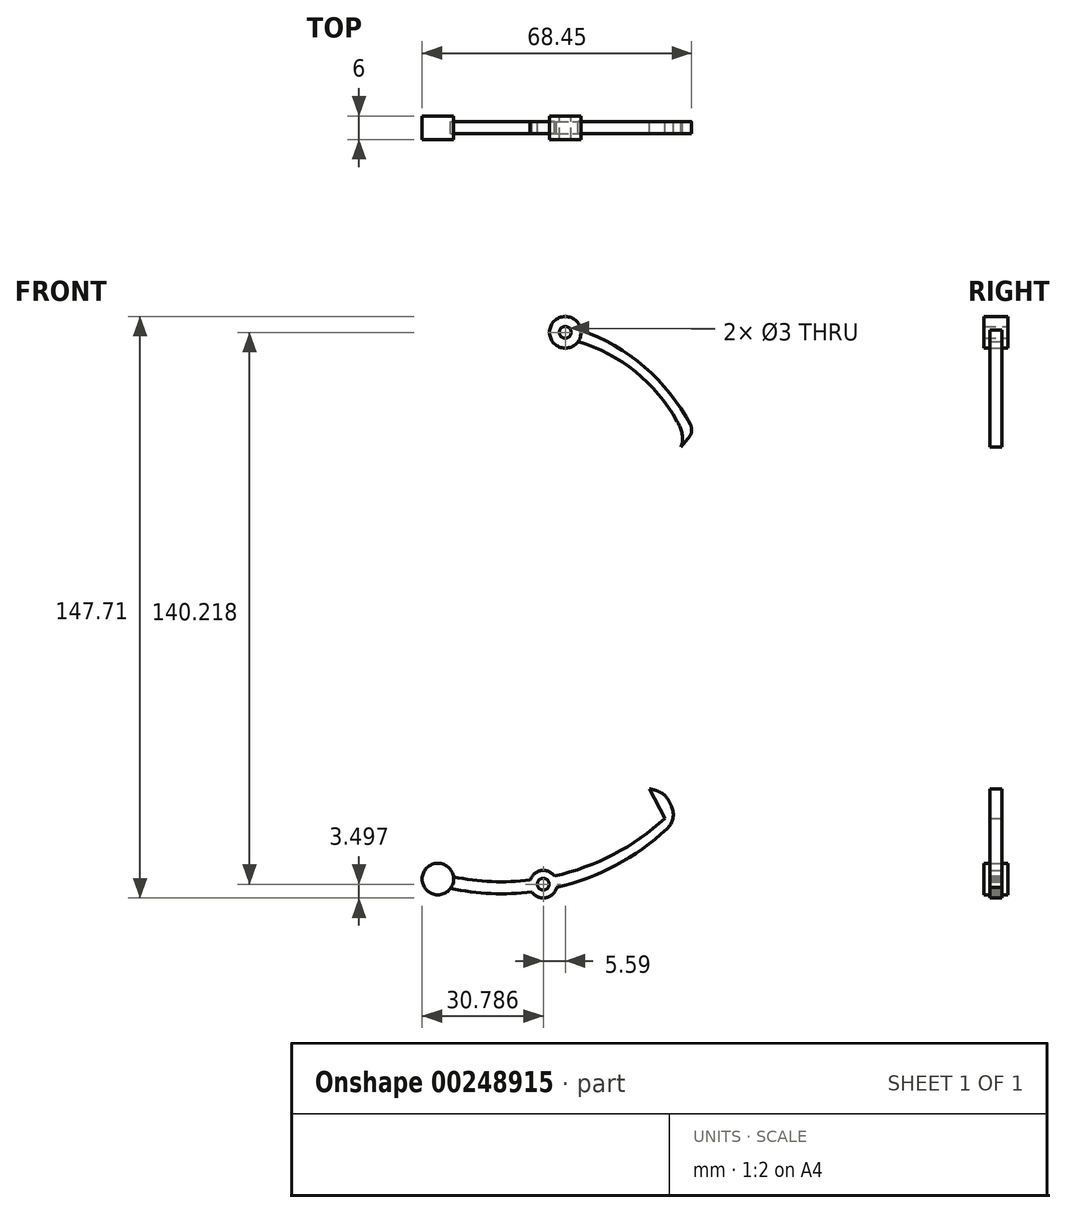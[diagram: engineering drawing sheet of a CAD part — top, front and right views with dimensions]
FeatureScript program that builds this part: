
annotation { "Feature Type Name" : "Feature", "Feature Type Description" : "" }
export const myFeature = defineFeature(function(context is Context, id is Id, definition is map)
    precondition{}
    {
        {
            var Q0;
            Q0=qCreatedBy(makeId("Front.planeOp"),FACE);
            var sketch = newSketch(context, id + "F0", { "sketchPlane" : qUnion([Q0])});
            skLineSegment(sketch, "E0", {"start": v(16.93, -54.43) * mm, "end": v(16.97, -54.42) * mm});
            skPoint(sketch, "E1.center", {"position": v(-0.03, 0) * mm});
            skLineSegment(sketch, "E2", {"start": v(0, 0) * mm, "end": v(-0.03, 0) * mm});
            skLineSegment(sketch, "E3", {"start": v(48.74, -18.05) * mm, "end": v(53.43, -19.79) * mm});
            skLineSegment(sketch, "E4", {"start": v(53.43, -19.79) * mm, "end": v(43.92, -27.8) * mm});
            skLineSegment(sketch, "E5.1.0", {"start": v(43.92, -27.8) * mm, "end": v(48.14, -30.47) * mm});
            skLineSegment(sketch, "E5.1.1", {"start": v(48.14, -30.47) * mm, "end": v(37.18, -36.33) * mm});
            skLineSegment(sketch, "E5.2.0", {"start": v(37.18, -36.33) * mm, "end": v(40.76, -39.82) * mm});
            skLineSegment(sketch, "E5.2.1", {"start": v(40.76, -39.82) * mm, "end": v(28.81, -43.27) * mm});
            skLineSegment(sketch, "E5.3.0", {"start": v(28.81, -43.27) * mm, "end": v(31.59, -47.43) * mm});
            skLineSegment(sketch, "E5.3.1", {"start": v(31.59, -47.43) * mm, "end": v(31.55, -47.43) * mm});
            skLineSegment(sketch, "E5.4.0", {"start": v(19.19, -48.32) * mm, "end": v(21.03, -52.96) * mm});
            skLineSegment(sketch, "E5.4.1", {"start": v(21.03, -52.96) * mm, "end": v(8.72, -51.26) * mm});
            skLineSegment(sketch, "E5.5.0", {"start": v(8.72, -51.26) * mm, "end": v(9.56, -56.19) * mm});
            skLineSegment(sketch, "E5.5.1", {"start": v(9.56, -56.19) * mm, "end": v(-2.13, -51.96) * mm});
            skLineSegment(sketch, "E5.6.0", {"start": v(-2.13, -51.96) * mm, "end": v(-2.33, -56.95) * mm});
            skLineSegment(sketch, "E5.6.1", {"start": v(-2.33, -56.95) * mm, "end": v(-12.89, -50.39) * mm});
            skLineSegment(sketch, "E5.7.0", {"start": v(-12.88, -50.39) * mm, "end": v(-14.12, -55.23) * mm});
            skLineSegment(sketch, "E5.7.1", {"start": v(-14.12, -55.23) * mm, "end": v(-23.08, -46.61) * mm});
            skLineSegment(sketch, "E5.8.0", {"start": v(-23.08, -46.61) * mm, "end": v(-25.3, -51.1) * mm});
            skLineSegment(sketch, "E5.8.1", {"start": v(-25.3, -51.1) * mm, "end": v(-32.27, -40.8) * mm});
            skLineSegment(sketch, "E5.9.0", {"start": v(-32.27, -40.8) * mm, "end": v(-35.37, -44.72) * mm});
            skLineSegment(sketch, "E5.9.1", {"start": v(-35.37, -44.72) * mm, "end": v(-40.05, -33.2) * mm});
            skLineSegment(sketch, "E5.10.0", {"start": v(-40.05, -33.2) * mm, "end": v(-43.9, -36.4) * mm});
            skLineSegment(sketch, "E5.10.1", {"start": v(-43.9, -36.4) * mm, "end": v(-46.08, -24.16) * mm});
            skLineSegment(sketch, "E5.11.0", {"start": v(-46.08, -24.16) * mm, "end": v(-50.5, -26.49) * mm});
            skLineSegment(sketch, "E5.11.1", {"start": v(-50.5, -26.49) * mm, "end": v(-50.1, -14.06) * mm});
            skLineSegment(sketch, "E5.12.0", {"start": v(-50.1, -14.06) * mm, "end": v(-54.9, -15.41) * mm});
            skLineSegment(sketch, "E5.12.1", {"start": v(-54.9, -15.41) * mm, "end": v(-51.92, -3.34) * mm});
            skLineSegment(sketch, "E5.13.0", {"start": v(-51.92, -3.34) * mm, "end": v(-56.91, -3.67) * mm});
            skLineSegment(sketch, "E5.13.1", {"start": v(-56.91, -3.67) * mm, "end": v(-51.48, 7.52) * mm});
            skLineSegment(sketch, "E5.14.0", {"start": v(-51.48, 7.52) * mm, "end": v(-56.43, 8.24) * mm});
            skLineSegment(sketch, "E5.14.1", {"start": v(-56.43, 8.24) * mm, "end": v(-48.8, 18.05) * mm});
            skLineSegment(sketch, "E5.15.0", {"start": v(-48.8, 18.05) * mm, "end": v(-53.49, 19.79) * mm});
            skLineSegment(sketch, "E5.15.1", {"start": v(-53.49, 19.79) * mm, "end": v(-43.98, 27.8) * mm});
            skLineSegment(sketch, "E5.16.0", {"start": v(-43.98, 27.8) * mm, "end": v(-48.2, 30.47) * mm});
            skLineSegment(sketch, "E5.16.1", {"start": v(-48.2, 30.47) * mm, "end": v(-37.24, 36.33) * mm});
            skLineSegment(sketch, "E5.17.0", {"start": v(-37.24, 36.33) * mm, "end": v(-40.82, 39.82) * mm});
            skLineSegment(sketch, "E5.17.1", {"start": v(-40.82, 39.82) * mm, "end": v(-28.87, 43.27) * mm});
            skLineSegment(sketch, "E5.18.0", {"start": v(-28.87, 43.27) * mm, "end": v(-31.65, 47.43) * mm});
            skLineSegment(sketch, "E5.18.1", {"start": v(-31.65, 47.43) * mm, "end": v(-19.24, 48.32) * mm});
            skLineSegment(sketch, "E5.19.0", {"start": v(-19.25, 48.32) * mm, "end": v(-21.1, 52.96) * mm});
            skLineSegment(sketch, "E5.19.1", {"start": v(-21.1, 52.96) * mm, "end": v(-8.78, 51.26) * mm});
            skLineSegment(sketch, "E5.20.0", {"start": v(-8.78, 51.26) * mm, "end": v(-9.62, 56.19) * mm});
            skLineSegment(sketch, "E5.20.1", {"start": v(-9.62, 56.19) * mm, "end": v(2.07, 51.96) * mm});
            skLineSegment(sketch, "E5.21.0", {"start": v(2.07, 51.96) * mm, "end": v(2.27, 56.95) * mm});
            skLineSegment(sketch, "E5.24.0", {"start": v(32.2, 40.8) * mm, "end": v(32.21, 40.8) * mm});
            skLineSegment(sketch, "E5.25.1", {"start": v(43.83, 36.4) * mm, "end": v(46.02, 24.16) * mm});
            skLineSegment(sketch, "E5.26.0", {"start": v(46.02, 24.16) * mm, "end": v(50.44, 26.49) * mm});
            skLineSegment(sketch, "E5.26.1", {"start": v(50.44, 26.49) * mm, "end": v(50.03, 14.06) * mm});
            skLineSegment(sketch, "E5.27.0", {"start": v(50.03, 14.06) * mm, "end": v(54.85, 15.41) * mm});
            skLineSegment(sketch, "E5.27.1", {"start": v(54.85, 15.41) * mm, "end": v(51.86, 3.34) * mm});
            skLineSegment(sketch, "E5.28.0", {"start": v(51.86, 3.34) * mm, "end": v(56.85, 3.67) * mm});
            skLineSegment(sketch, "E5.28.1", {"start": v(56.85, 3.67) * mm, "end": v(51.42, -7.52) * mm});
            skLineSegment(sketch, "E5.29.0", {"start": v(51.42, -7.52) * mm, "end": v(56.37, -8.24) * mm});
            skLineSegment(sketch, "E5.29.1", {"start": v(56.37, -8.24) * mm, "end": v(48.74, -18.05) * mm});
            skLineSegment(sketch, "E6", {"start": v(30.07, -45.16) * mm, "end": v(31.59, -47.43) * mm});
            skPoint(sketch, "E7.visualSharp", {"position": v(30.07, -45.1) * mm});
            skPoint(sketch, "E8.orphan", {"position": v(-17.75, -71.35) * mm});
            skPoint(sketch, "E9.orphan", {"position": v(-12.5, -69.02) * mm});
            skLineSegment(sketch, "E10", {"start": v(-0.03, 0) * mm, "end": v(0, 0.04) * mm});
            skArc(sketch, "E11", {"start": v(35.3, 44.72) * mm, "mid": v(35.3, 44.73) * mm, "end": v(35.3, 44.73) * mm});
            skPoint(sketch, "E12.startSnap0", {"position": v(33.76, 42.76) * mm});
            skLineSegment(sketch, "E13", {"start": v(32.2, 40.8) * mm, "end": v(32.2, 40.82) * mm});
            skLineSegment(sketch, "E14.trimOffspring", {"start": v(32.2, 40.8) * mm, "end": v(34.76, 44.04) * mm});
            skPoint(sketch, "E15.orphan", {"position": v(33.76, 42.78) * mm});
            skArc(sketch, "E16", {"start": v(32.2, 40.8) * mm, "mid": v(32.49, 44.15) * mm, "end": v(31.2, 47.25) * mm});
            skArc(sketch, "E17", {"start": v(34.76, 44.04) * mm, "mid": v(34.87, 45.2) * mm, "end": v(34.7, 46.34) * mm});
            skPoint(sketch, "E18.orphan", {"position": v(0, 68.5) * mm});
            skLineSegment(sketch, "E19.trimOffspring", {"start": v(0, 52.7) * mm, "end": v(0, -52.73) * mm});
            skLineSegment(sketch, "E20", {"start": v(-0.03, -659.94) * mm, "end": v(-0.03, -418) * mm, "construction": true});
            skLineSegment(sketch, "E21", {"start": v(-0.03, -637.8) * mm, "end": v(-0.03, -380.4) * mm});
            skCircle(sketch, "E22", {"center": v(-0.03, 300) * mm, "radius": 63.36 * mm});
            skLineSegment(sketch, "E23", {"start": v(-2.33, -56.95) * mm, "end": v(2.27, 56.95) * mm});
            skCircle(sketch, "E24", {"center": v(-2.8, -70.24) * mm, "radius": 1.5 * mm});
            skArc(sketch, "E25", {"start": v(-5.7, -72.2) * mm, "mid": v(-2.18, -73.69) * mm, "end": v(0.6, -71.08) * mm});
            skLineSegment(sketch, "E26", {"start": v(0, 0.04) * mm, "end": v(28.81, -43.27) * mm});
            skLineSegment(sketch, "E27", {"start": v(0, 0.04) * mm, "end": v(19.19, -48.32) * mm});
            skLineSegment(sketch, "E28", {"start": v(0, 0.04) * mm, "end": v(24.13, -46.04) * mm});
            skLineSegment(sketch, "E29", {"start": v(0, 0.04) * mm, "end": v(15.95, -56.94) * mm});
            skLineSegment(sketch, "E30.trimOffspring", {"start": v(19.19, -48.32) * mm, "end": v(19.18, -48.32) * mm});
            skLineSegment(sketch, "E31", {"start": v(24.22, -46) * mm, "end": v(28.14, -53.47) * mm});
            skArc(sketch, "E32", {"start": v(27.7, -47.15) * mm, "mid": v(26, -46.48) * mm, "end": v(24.22, -46) * mm});
            skArc(sketch, "E33", {"start": v(30.85, -54) * mm, "mid": v(29.75, -50.36) * mm, "end": v(27.7, -47.15) * mm});
            skCircle(sketch, "E34", {"center": v(-29.58, -68.93) * mm, "radius": 4 * mm});
            skArc(sketch, "E35.trimOffspring", {"start": v(0.02, -68.16) * mm, "mid": v(15.05, -62.68) * mm, "end": v(28.14, -53.47) * mm});
            skArc(sketch, "E36.trimOffspring", {"start": v(0.6, -71.08) * mm, "mid": v(16.96, -64.72) * mm, "end": v(30.85, -54) * mm});
            skArc(sketch, "E37.trimOffspring", {"start": v(0.02, -68.16) * mm, "mid": v(-3.38, -66.8) * mm, "end": v(-6.14, -69.2) * mm});
            skArc(sketch, "E38.trimOffspring", {"start": v(-25.62, -68.35) * mm, "mid": v(-15.91, -69.56) * mm, "end": v(-6.14, -69.2) * mm});
            skArc(sketch, "E39.trimOffspring", {"start": v(-26.34, -71.28) * mm, "mid": v(-16.06, -72.6) * mm, "end": v(-5.7, -72.2) * mm});
            skCircle(sketch, "E40", {"center": v(-29.58, -68.93) * mm, "radius": 3 * mm});
            skCircle(sketch, "E41", {"center": v(2.8, 69.97) * mm, "radius": 4 * mm});
            skCircle(sketch, "E42", {"center": v(2.8, 69.97) * mm, "radius": 1.5 * mm});
            skArc(sketch, "E43", {"start": v(31.2, 47.25) * mm, "mid": v(20.65, 59.94) * mm, "end": v(6.03, 67.62) * mm});
            skArc(sketch, "E44", {"start": v(34.7, 46.34) * mm, "mid": v(23, 61.07) * mm, "end": v(6.76, 70.54) * mm});
            skPoint(sketch, "E45.orphan", {"position": v(0, 71.5) * mm});
            skPoint(sketch, "E46.orphan", {"position": v(2.52, 68.5) * mm});
            skLineSegment(sketch, "E47.trimOffspring", {"start": v(32.2, 40.8) * mm, "end": v(32.2, 40.8) * mm});
            skLineSegment(sketch, "E48", {"start": v(2.8, 69.97) * mm, "end": v(32.21, 40.8) * mm, "construction": true});
            skSolve(sketch);
        }
        {
            var Q0;
            Q0=makeQuery(id+"F0.imprint","IMPRINT",FACE,{"disambiguationData":[TD([[makeQuery(id+"F0.imprint","IMPRINT",EDGE,{"derivedFrom":sQuery(id+"F0.wireOp",EDGE,"E24")}),-1.0]])]});
            extrude(context, id + "F1", {"entities" : qUnion([Q0]), "endBound" : BoundingType.SYMMETRIC, "depth" : 3 * mm});
        }
        {
            var Q0;
            Q0=makeQuery(id+"F0.imprint","IMPRINT",FACE,{"disambiguationData":[TD([[makeQuery(id+"F0.imprint","IMPRINT",EDGE,{"derivedFrom":sQuery(id+"F0.wireOp",EDGE,"E40")}),-1.0]])]});
            extrude(context, id + "F2", {"entities" : qUnion([Q0]), "operationType" : NewBodyOperationType.ADD, "endBound" : BoundingType.SYMMETRIC, "depth" : 6 * mm});
        }
        {
            var Q0;
            Q0=makeQuery(id+"F0.imprint","IMPRINT",FACE,{"disambiguationData":[TD([[makeQuery(id+"F0.imprint","IMPRINT",EDGE,{"derivedFrom":sQuery(id+"F0.wireOp",EDGE,"E40")}),1.0]])]});
            extrude(context, id + "F3", {"entities" : qUnion([Q0]), "operationType" : NewBodyOperationType.ADD, "endBound" : BoundingType.SYMMETRIC, "depth" : 6 * mm});
        }
        {
            var Q0;
            Q0=makeQuery(id+"F1.opExtrude","SWEPT_EDGE",EDGE,{"disambiguationData":[OSD([sQuery(id+"F0.wireOp",EDGE,"E33"),sQuery(id+"F0.wireOp",EDGE,"E36.trimOffspring")])]});
            var Q1;
            Q1=makeQuery(id+"F1.opExtrude","SWEPT_EDGE",EDGE,{"disambiguationData":[OSD([sQuery(id+"F0.wireOp",EDGE,"E32"),sQuery(id+"F0.wireOp",EDGE,"E33")])]});
            fillet(context, id + "F4", {"entities" : qUnion([Q0, Q1]), "radius" : 5 * mm, "tangentPropagation" : true, "allowEdgeOverflow" : false});
        }
        {
            var Q0;
            {var subQ3=sQuery(id+"F0.wireOp",EDGE,"E17");Q0=makeQuery(id+"F0.imprint","IMPRINT",FACE,{"disambiguationData":[TD([[makeQuery(id+"F0.imprint","IMPRINT",EDGE,{"derivedFrom":subQ3}),1.0]])]});}
            extrude(context, id + "F5", {"entities" : qUnion([Q0]), "endBound" : BoundingType.SYMMETRIC, "depth" : 3 * mm});
        }
        {
            var Q0;
            Q0=makeQuery(id+"F0.imprint","IMPRINT",FACE,{"disambiguationData":[TD([[makeQuery(id+"F0.imprint","IMPRINT",EDGE,{"derivedFrom":sQuery(id+"F0.wireOp",EDGE,"E42")}),-1.0]])]});
            extrude(context, id + "F6", {"entities" : qUnion([Q0]), "operationType" : NewBodyOperationType.ADD, "endBound" : BoundingType.SYMMETRIC, "depth" : 6 * mm});
        }
        {
            var Q0;
            Q0=makeQuery(id+"F5.opExtrude","SWEPT_EDGE",EDGE,{"disambiguationData":[OSD([sQuery(id+"F0.wireOp",EDGE,"E17"),sQuery(id+"F0.wireOp",EDGE,"E44")])]});
            var Q1;
            Q1=makeQuery(id+"F5.opExtrude","SWEPT_EDGE",EDGE,{"disambiguationData":[OSD([sQuery(id+"F0.wireOp",EDGE,"E14.trimOffspring"),sQuery(id+"F0.wireOp",EDGE,"E17")])]});
            var Q2;
            Q2=makeQuery(id+"F5.opExtrude","SWEPT_EDGE",EDGE,{"disambiguationData":[OSD([sQuery(id+"F0.wireOp",EDGE,"E16"),sQuery(id+"F0.wireOp",EDGE,"E43")])]});
            fillet(context, id + "F7", {"entities" : qUnion([Q0, Q1, Q2]), "radius" : 2 * mm, "tangentPropagation" : true, "allowEdgeOverflow" : false});
        }
    });
